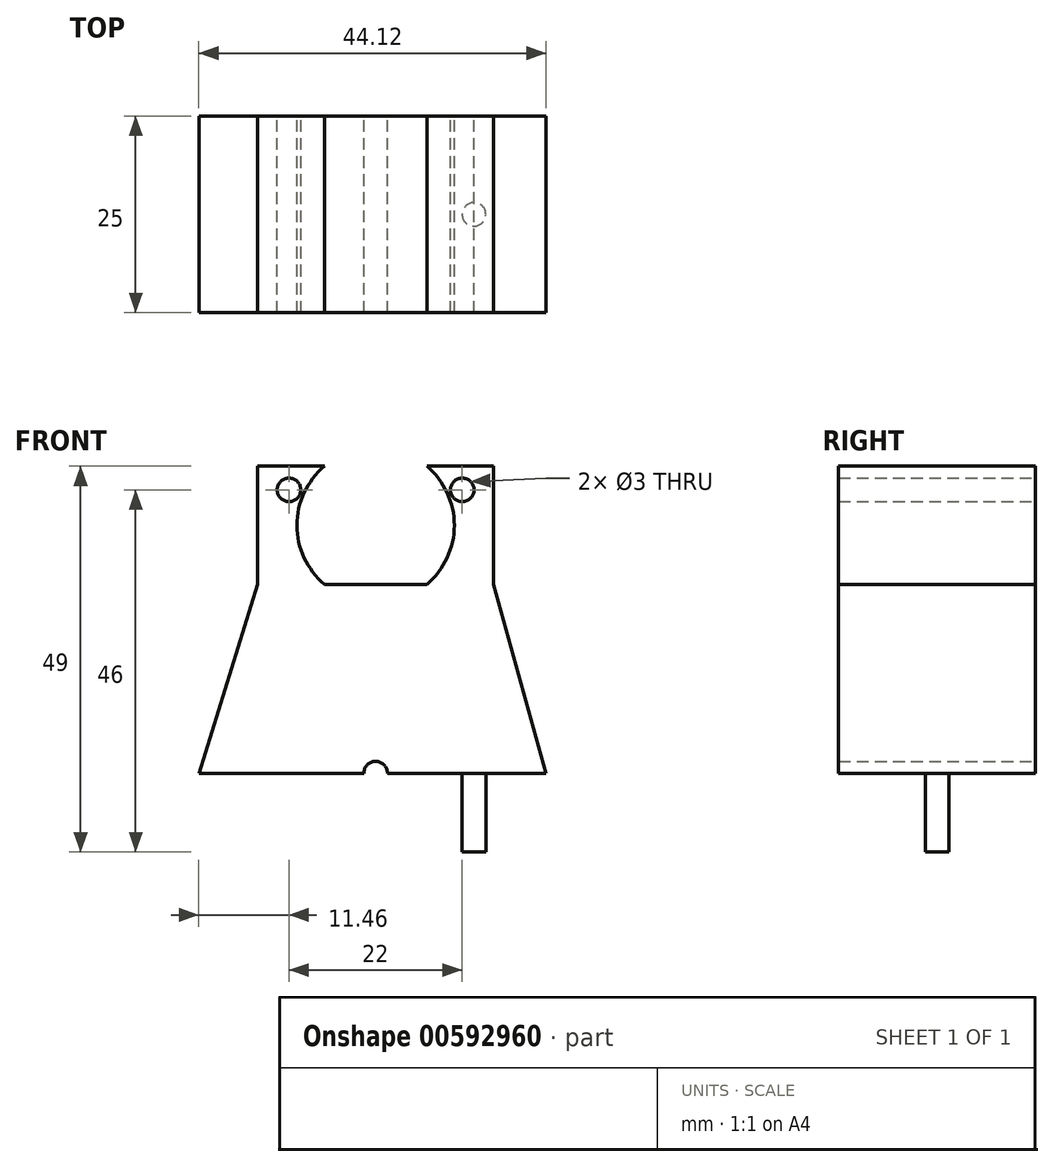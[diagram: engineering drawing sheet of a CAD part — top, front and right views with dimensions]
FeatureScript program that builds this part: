
annotation { "Feature Type Name" : "Feature", "Feature Type Description" : "" }
export const myFeature = defineFeature(function(context is Context, id is Id, definition is map)
    precondition{}
    {
        {
            var Q0;
            Q0=qCreatedBy(makeId("Front.planeOp"),FACE);
            var sketch = newSketch(context, id + "F0", { "sketchPlane" : qUnion([Q0])});
            skLineSegment(sketch, "E0", {"start": v(-25.56, 0) * mm, "end": v(24.44, 0) * mm});
            skLineSegment(sketch, "E1", {"start": v(-15, 34) * mm, "end": v(15, 34) * mm});
            skLineSegment(sketch, "E2", {"start": v(-25.56, 0) * mm, "end": v(-15, 34) * mm});
            skLineSegment(sketch, "E3", {"start": v(15, 34) * mm, "end": v(24.44, 0) * mm});
            skLineSegment(sketch, "E4", {"start": v(-15, 34) * mm, "end": v(-15, 49) * mm});
            skLineSegment(sketch, "E5", {"start": v(-15, 49) * mm, "end": v(15, 49) * mm, "construction": true});
            skLineSegment(sketch, "E6", {"start": v(15, 49) * mm, "end": v(15, 34) * mm});
            skLineSegment(sketch, "E7", {"start": v(6.5, 49) * mm, "end": v(6.5, 34) * mm, "construction": true});
            skLineSegment(sketch, "E8", {"start": v(-6.5, 49) * mm, "end": v(-6.5, 34) * mm, "construction": true});
            skArc(sketch, "E9", {"start": v(-6.5, 49) * mm, "mid": v(-10, 41.5) * mm, "end": v(-6.5, 34) * mm});
            skArc(sketch, "E10", {"start": v(6.5, 34) * mm, "mid": v(10, 41.5) * mm, "end": v(6.5, 49) * mm});
            skLineSegment(sketch, "E11", {"start": v(-10, 41.5) * mm, "end": v(10, 41.5) * mm, "construction": true});
            skLineSegment(sketch, "E12", {"start": v(-15, 49) * mm, "end": v(-6.5, 49) * mm});
            skLineSegment(sketch, "E13", {"start": v(6.5, 49) * mm, "end": v(15, 49) * mm});
            skCircle(sketch, "E14", {"center": v(0, 10) * mm, "radius": 1.5 * mm});
            skCircle(sketch, "E15", {"center": v(-11, 46) * mm, "radius": 1.5 * mm});
            skCircle(sketch, "E16", {"center": v(11, 46) * mm, "radius": 1.5 * mm});
            skSolve(sketch);
        }
        {
            var Q0;
            {var subQ0=sQuery(id+"F0.wireOp",EDGE,"E6");Q0=makeQuery(id+"F0.imprint","IMPRINT",FACE,{"disambiguationData":[TD([[makeQuery(id+"F0.imprint","IMPRINT",EDGE,{"derivedFrom":subQ0}),-1.0]])]});}
            var Q1;
            {var subQ0=sQuery(id+"F0.wireOp",EDGE,"E4");Q1=makeQuery(id+"F0.imprint","IMPRINT",FACE,{"disambiguationData":[TD([[makeQuery(id+"F0.imprint","IMPRINT",EDGE,{"derivedFrom":subQ0}),-1.0]])]});}
            var Q2;
            Q2=makeQuery(id+"F0.imprint","IMPRINT",FACE,{"disambiguationData":[TD([[makeQuery(id+"F0.imprint","IMPRINT",EDGE,{"derivedFrom":sQuery(id+"F0.wireOp",EDGE,"E0")}),1.0]])]});
            extrude(context, id + "F1", {"entities" : qUnion([Q0, Q1, Q2]), "depth" : 25 * mm, "offsetDistance" : 25 * mm});
        }
        {
            var Q0;
            Q0=makeQuery(id+"F1.opExtrude","SWEPT_FACE",FACE,{"disambiguationData":[OSD([sQuery(id+"F0.wireOp",EDGE,"E0")])]});
            var sketch = newSketch(context, id + "F2", { "sketchPlane" : qUnion([Q0])});
            skLineSegment(sketch, "E17", {"start": v(0, 25) * mm, "end": v(0, 0) * mm, "construction": true});
            skCircle(sketch, "E18", {"center": v(-12.5, 12.5) * mm, "radius": 1.5 * mm});
            skPoint(sketch, "E18.centerSnap0", {"position": v(0, 12.5) * mm});
            skCircle(sketch, "E19.MirrorC", {"center": v(12.5, 12.5) * mm, "radius": 1.5 * mm});
            skSolve(sketch);
        }
        {
            var Q0;
            Q0=makeQuery(id+"F2.imprint","IMPRINT",FACE,{"disambiguationData":[TD([[makeQuery(id+"F2.imprint","IMPRINT",EDGE,{"derivedFrom":sQuery(id+"F2.wireOp",EDGE,"E18")}),1.0]])]});
            var Q1;
            Q1=makeQuery(id+"F2.imprint","IMPRINT",FACE,{"disambiguationData":[TD([[makeQuery(id+"F2.imprint","IMPRINT",EDGE,{"derivedFrom":sQuery(id+"F2.wireOp",EDGE,"E19.MirrorC")}),-1.0]])]});
            extrude(context, id + "F3", {"entities" : qUnion([Q0, Q1]), "operationType" : NewBodyOperationType.REMOVE, "oppositeDirection" : true, "depth" : 10 * mm, "offsetDistance" : 25 * mm});
        }
    });
